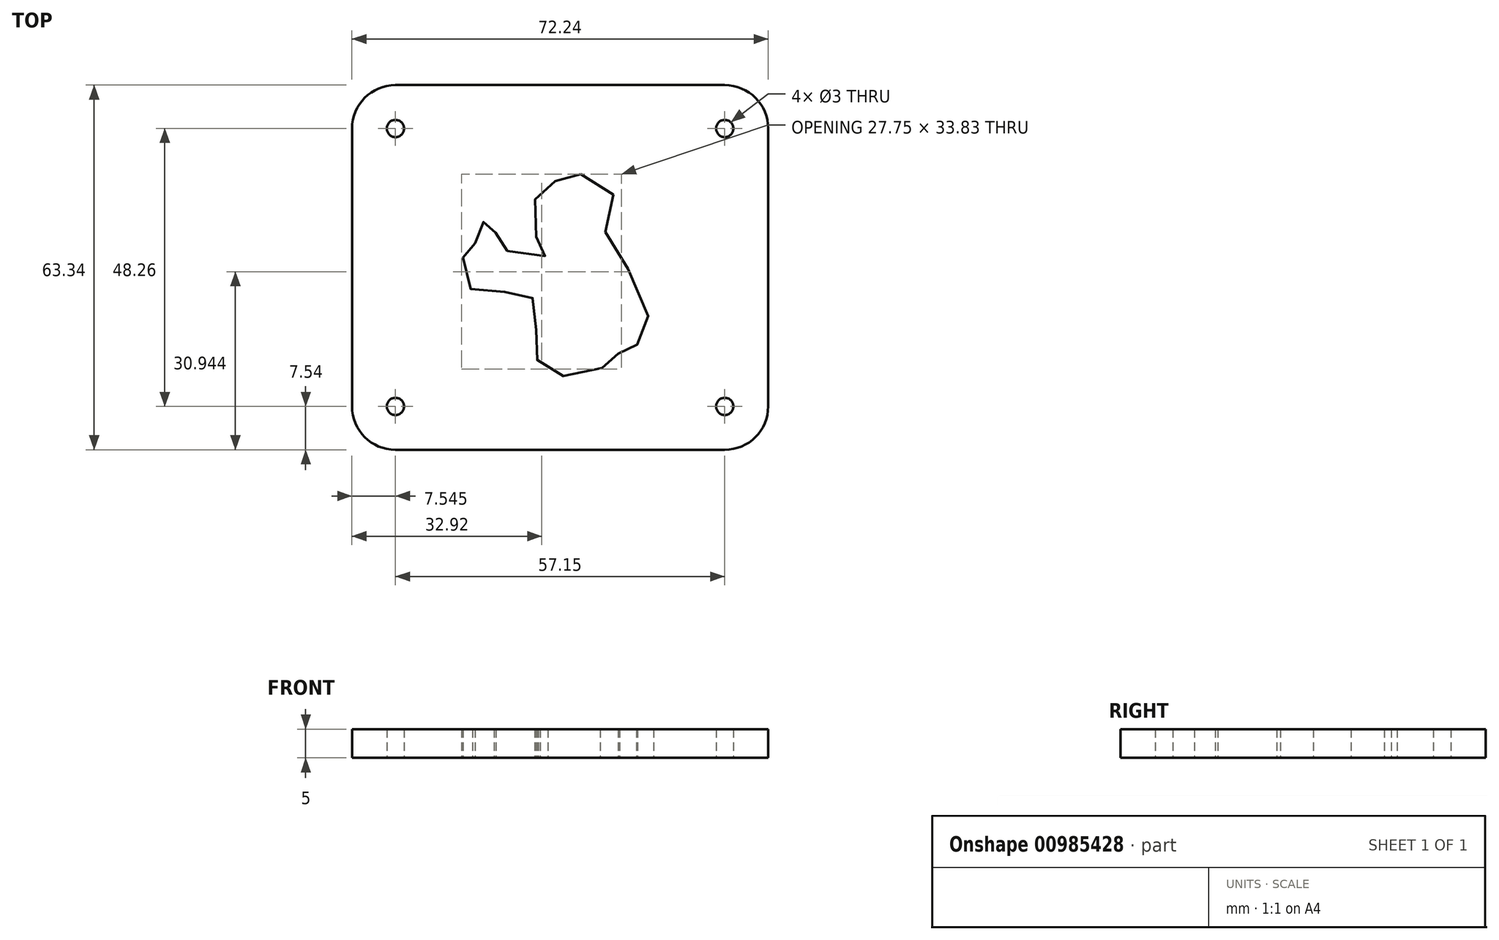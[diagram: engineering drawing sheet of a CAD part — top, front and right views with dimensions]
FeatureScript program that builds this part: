
annotation { "Feature Type Name" : "Feature", "Feature Type Description" : "" }
export const myFeature = defineFeature(function(context is Context, id is Id, definition is map)
    precondition{}
    {
        {
            var Q0;
            Q0=qCreatedBy(makeId("Top.planeOp"),FACE);
            var sketch = newSketch(context, id + "F0", { "sketchPlane" : qUnion([Q0])});
            skLineSegment(sketch, "E0.bottom", {"start": v(28.58, 31.67) * mm, "end": v(-28.58, 31.67) * mm});
            skLineSegment(sketch, "E0.top", {"start": v(28.58, -31.67) * mm, "end": v(-28.58, -31.67) * mm});
            skLineSegment(sketch, "E0.left", {"start": v(36.12, 24.13) * mm, "end": v(36.12, -24.13) * mm});
            skLineSegment(sketch, "E0.right", {"start": v(-36.12, 24.13) * mm, "end": v(-36.12, -24.13) * mm});
            skPoint(sketch, "E0.middle", {"position": v(0, 0) * mm});
            skPoint(sketch, "E1.visualSharp", {"position": v(-36.12, 31.67) * mm});
            skArc(sketch, "E1.filletArc", {"start": v(-28.58, 31.67) * mm, "mid": v(-33.9, 29.46) * mm, "end": v(-36.12, 24.13) * mm});
            skPoint(sketch, "E2.visualSharp", {"position": v(36.12, 31.67) * mm});
            skArc(sketch, "E2.filletArc", {"start": v(36.12, 24.13) * mm, "mid": v(33.9, 29.46) * mm, "end": v(28.58, 31.67) * mm});
            skPoint(sketch, "E3.visualSharp", {"position": v(36.12, -31.67) * mm});
            skArc(sketch, "E3.filletArc", {"start": v(28.58, -31.67) * mm, "mid": v(33.9, -29.46) * mm, "end": v(36.12, -24.13) * mm});
            skPoint(sketch, "E4.visualSharp", {"position": v(-36.12, -31.67) * mm});
            skArc(sketch, "E4.filletArc", {"start": v(-36.12, -24.13) * mm, "mid": v(-33.9, -29.46) * mm, "end": v(-28.58, -31.67) * mm});
            skCircle(sketch, "E5", {"center": v(-28.58, -24.13) * mm, "radius": 1.5 * mm});
            skCircle(sketch, "E6", {"center": v(28.58, -24.13) * mm, "radius": 1.5 * mm});
            skCircle(sketch, "E7", {"center": v(28.58, 24.13) * mm, "radius": 1.5 * mm});
            skCircle(sketch, "E8", {"center": v(-28.58, 24.13) * mm, "radius": 1.5 * mm});
            skFitSpline(sketch, "E9", {"points": [v(3.6, 16.19) * mm, v(0, 14.14) * mm, v(-1.3, 15.28) * mm, v(-4.38, 12.77) * mm, v(-3.46, 9.12) * mm, v(-4.03, 3.76) * mm, v(-2.1, 2.27) * mm, v(-5.86, 1.82) * mm, v(-9.97, 3.3) * mm, v(-11.45, 4.55) * mm, v(-11.1, 6.72) * mm, v(-11.8, 8.2) * mm, v(-13.39, 7.86) * mm, v(-15.21, 5.35) * mm, v(-14.76, 4.21) * mm, v(-16.87, 3.87) * mm, v(-16.87, 2.04) * mm, v(-16.87, -2.3) * mm, v(-13.5, -4.46) * mm, v(-9.5, -4.23) * mm, v(-5.29, -4.23) * mm, v(-4.72, -6.62) * mm, v(-4.26, -10.39) * mm, v(-3.8, -13.7) * mm, v(-3.8, -16.55) * mm, v(-0.37, -18.7) * mm, v(1.9, -18.7) * mm, v(8.74, -17.12) * mm, v(10.34, -16.2) * mm, v(10.11, -14.84) * mm, v(12.28, -15.18) * mm, v(13.42, -12.9) * mm, v(13.3, -11.53) * mm, v(16.13, -4.91) * mm, v(7.03, 4.1) * mm, v(9.88, 8.77) * mm, v(8.06, 14.25) * mm, v(3.6, 16.19) * mm]});
            skSolve(sketch);
        }
        {
            var Q0;
            Q0 = qSketchRegion(id + "F0", true);
            extrude(context, id + "F1", {"entities" : qUnion([Q0]), "depth" : 5 * mm, "offsetDistance" : 25 * mm});
        }
    });
